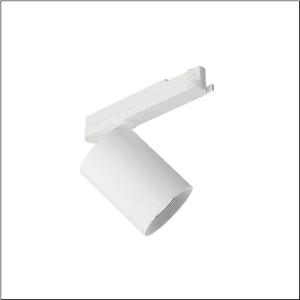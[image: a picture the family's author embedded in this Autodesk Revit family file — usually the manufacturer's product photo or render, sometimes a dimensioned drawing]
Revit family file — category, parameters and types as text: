
# Revit family: spot_21_51se14mbb5b
name_source: partatom
category: Lighting Fixtures
units: mm (PartAtom-declared; Revit-internal decimal feet)

## family parameters
Cut with Voids When Loaded = No
Host = Face
Light Source = No
Part Type = Normal
Room Calculation Point = No
Round Connector Dimension = Use Diameter
Shared = No

## types (1)
- --- (1 x LED, 5530 lm, 41.8 W, 3000K)
    Apparent Load = 42 VA
    CIE Flux Codes = 96 99 100 100 100
    Color Rendering = 90
    Color Temperature = 3000K
    Default Elevation = 1800 mm
    Description = Spot 21, directional spotlight, light control with lens, of PMMA, LED rated luminous flux: 5.110lm, light colour: 930, control gear: ECG Multilumen, with 3-phase adapter, mains connection: 220..240V, AC, 50/60Hz, of aluminium, traffic white (RAL 9016), length: 213mm, diameter: 105mm, protection rating (complete): IP20, insulation class (complete): insulation class I (protective earthing), certification: CE, impact resistance: IK02, permissible ambient temperature for indoor applications: -20..+40°C, packaging unit: 1 piece
    Height = 175 mm
    Lamp = 1 x LED
    Lamp Light Flux = 5530 lm
    Lamp Power = 41.8 W
    Lamp count = 1
    Length = 105 mm
    Luminous efficacy = 132 lm/W
    Manufacturer = Siteco
    ModVariant = No
    Model = 51SE14MBB5B
    Mounting Place = Ceiling
    Mounting Type = Pendant
    Number of Poles = 1
    OnlyDefault = Yes
    Power Factor = 1
    Product Name = Spot 21
    Product group = directional spotlight
    ProductGroupID = 905
    Protection Class = Protection class I
    Protection Degree = IP 20
    RLX_Detail_Level = 1
    RLX_Emergency_Light_Flux = 0 lm
    RLX_Emergency_Type = 0
    RLX_Emergency_Type_DB = No
    RlxData = <blob elided: 17669 chars, md5=9502f7f5>
    Socket = socket
    Standby Power = 0 W
    System Light Flux = 5530 lm
    System Power = 42 W
    Type Comments = factory setting: luminous flux: 100 % | (ON | ON | ON | ON) | 1050 mA
    Type Image = l_1003976.jpg
    URL = http://relux.com
    VarID = @adj_093137
    Voltage = 0 V
    Weight = 0.00 kg
    Width = 0 mm  [stored 0 ft]

note: [stored X ft] marks values corroborated as IEEE doubles in the binary element streams (Revit-internal decimal feet)

## geometry (parser evidence)
native form markers: Blend x4, Sweep x9
no freeform markers — native parametric forms only
